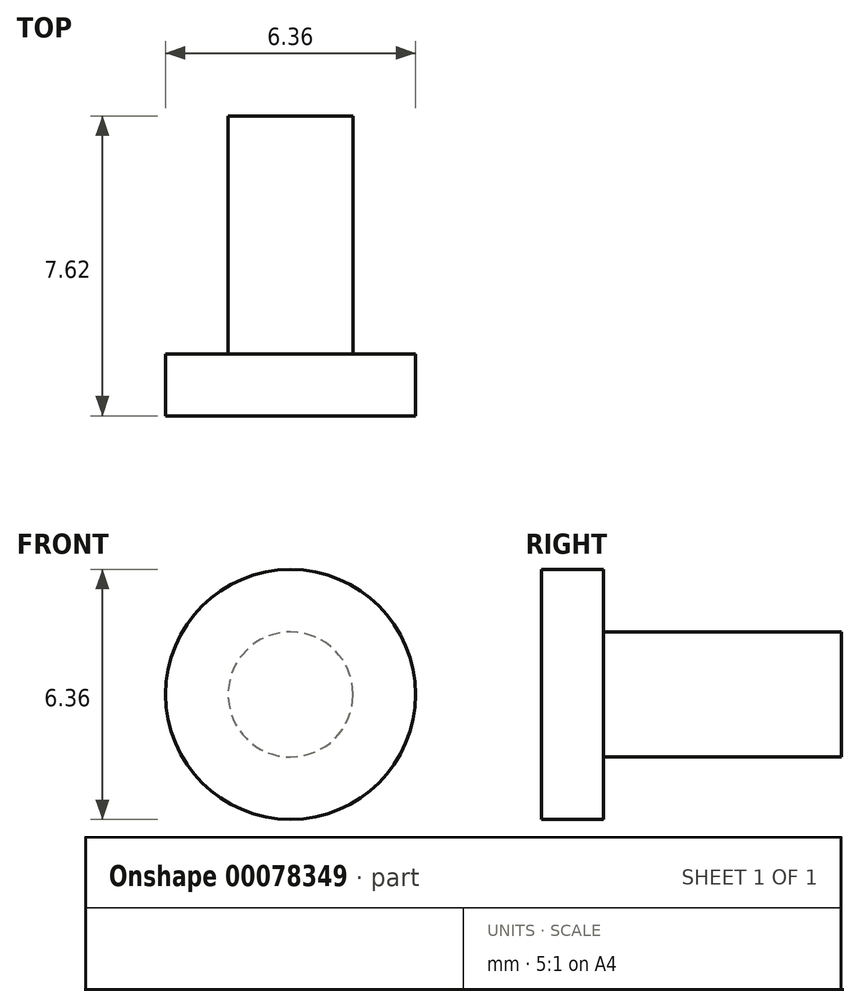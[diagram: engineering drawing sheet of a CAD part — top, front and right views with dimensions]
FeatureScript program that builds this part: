
annotation { "Feature Type Name" : "Feature", "Feature Type Description" : "" }
export const myFeature = defineFeature(function(context is Context, id is Id, definition is map)
    precondition{}
    {
        {
            var Q0;
            Q0=qCreatedBy(makeId("Right.planeOp"),FACE);
            var sketch = newSketch(context, id + "F0", { "sketchPlane" : qUnion([Q0])});
            skLineSegment(sketch, "E0", {"start": v(0, 0) * mm, "end": v(0, 3.18) * mm});
            skLineSegment(sketch, "E1", {"start": v(0, 3.18) * mm, "end": v(1.57, 3.18) * mm});
            skLineSegment(sketch, "E2", {"start": v(1.57, 3.18) * mm, "end": v(1.57, 1.59) * mm});
            skLineSegment(sketch, "E3", {"start": v(1.57, 1.59) * mm, "end": v(7.62, 1.59) * mm});
            skLineSegment(sketch, "E4", {"start": v(7.62, 1.59) * mm, "end": v(7.62, 0) * mm});
            skLineSegment(sketch, "E5", {"start": v(0, 0) * mm, "end": v(7.62, 0) * mm});
            skSolve(sketch);
        }
        {
            var Q0;
            Q0 = qSketchRegion(id + "F0", true);
            var Q1;
            Q1=sQuery(id+"F0.wireOp",EDGE,"E5");
            revolve(context, id + "F1", {"entities" : qUnion([Q0]), "axis" : qUnion([Q1]), "revolveType" : RevolveType.FULL});
        }
    });
